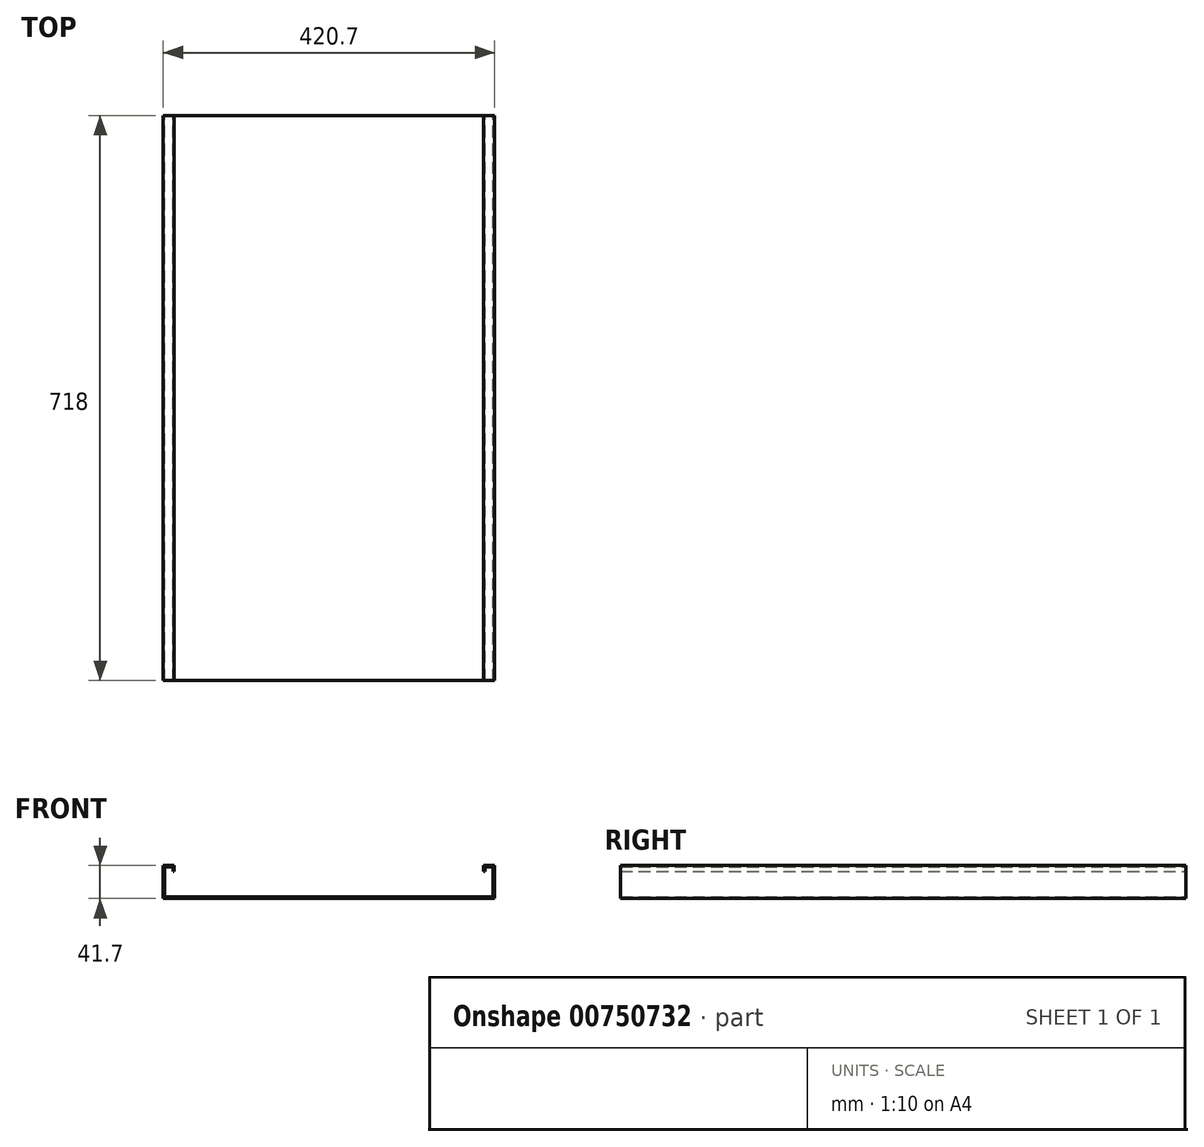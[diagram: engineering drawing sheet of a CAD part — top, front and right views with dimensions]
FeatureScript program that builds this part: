
annotation { "Feature Type Name" : "Feature", "Feature Type Description" : "" }
export const myFeature = defineFeature(function(context is Context, id is Id, definition is map)
    precondition{}
    {
        {
            var Q0;
            Q0=qCreatedBy(makeId("Front.planeOp"),FACE);
            var sketch = newSketch(context, id + "F0", { "sketchPlane" : qUnion([Q0])});
            skLineSegment(sketch, "E0", {"start": v(-210.35, 0.85) * mm, "end": v(-208.65, 0.85) * mm});
            skLineSegment(sketch, "E1", {"start": v(-208.65, 0.85) * mm, "end": v(-208.65, 39.15) * mm});
            skLineSegment(sketch, "E2", {"start": v(-208.65, 39.15) * mm, "end": v(-198.05, 39.15) * mm});
            skLineSegment(sketch, "E3", {"start": v(-198.05, 39.15) * mm, "end": v(-198.05, 33.65) * mm});
            skLineSegment(sketch, "E4", {"start": v(-198.05, 33.65) * mm, "end": v(-196.35, 33.65) * mm});
            skLineSegment(sketch, "E5", {"start": v(-196.35, 33.65) * mm, "end": v(-196.35, 40.85) * mm});
            skLineSegment(sketch, "E6", {"start": v(-196.35, 40.85) * mm, "end": v(-210.35, 40.85) * mm});
            skLineSegment(sketch, "E7", {"start": v(-210.35, 40.85) * mm, "end": v(-210.35, 0.85) * mm});
            skLineSegment(sketch, "E8", {"start": v(-203.35, 39.15) * mm, "end": v(-203.35, 40.85) * mm, "construction": true});
            skLineSegment(sketch, "E9.bottom", {"start": v(210.35, -0.85) * mm, "end": v(-210.35, -0.85) * mm});
            skLineSegment(sketch, "E9.top", {"start": v(210.35, 0.85) * mm, "end": v(-210.35, 0.85) * mm});
            skLineSegment(sketch, "E9.left", {"start": v(210.35, -0.85) * mm, "end": v(210.35, 0.85) * mm});
            skLineSegment(sketch, "E9.right", {"start": v(-210.35, -0.85) * mm, "end": v(-210.35, 0.85) * mm});
            skPoint(sketch, "E9.middle", {"position": v(0, 0) * mm});
            skLineSegment(sketch, "E10.MirrorCS", {"start": v(208.65, 0.85) * mm, "end": v(208.65, 39.15) * mm});
            skLineSegment(sketch, "E11.MirrorCS", {"start": v(208.65, 39.15) * mm, "end": v(198.05, 39.15) * mm});
            skLineSegment(sketch, "E12.MirrorCS", {"start": v(198.05, 39.15) * mm, "end": v(198.05, 33.65) * mm});
            skLineSegment(sketch, "E13.MirrorCS", {"start": v(198.05, 33.65) * mm, "end": v(196.35, 33.65) * mm});
            skLineSegment(sketch, "E14.MirrorCS", {"start": v(196.35, 33.65) * mm, "end": v(196.35, 40.85) * mm});
            skLineSegment(sketch, "E15.MirrorCS", {"start": v(196.35, 40.85) * mm, "end": v(210.35, 40.85) * mm});
            skLineSegment(sketch, "E16.MirrorCS", {"start": v(210.35, 40.85) * mm, "end": v(210.35, 0.85) * mm});
            skSolve(sketch);
        }
        {
            var Q0;
            Q0 = qSketchRegion(id + "F0", true);
            extrude(context, id + "F1", {"entities" : qUnion([Q0]), "endBound" : BoundingType.SYMMETRIC, "depth" : 718 * mm, "offsetDistance" : 25 * mm});
        }
    });
